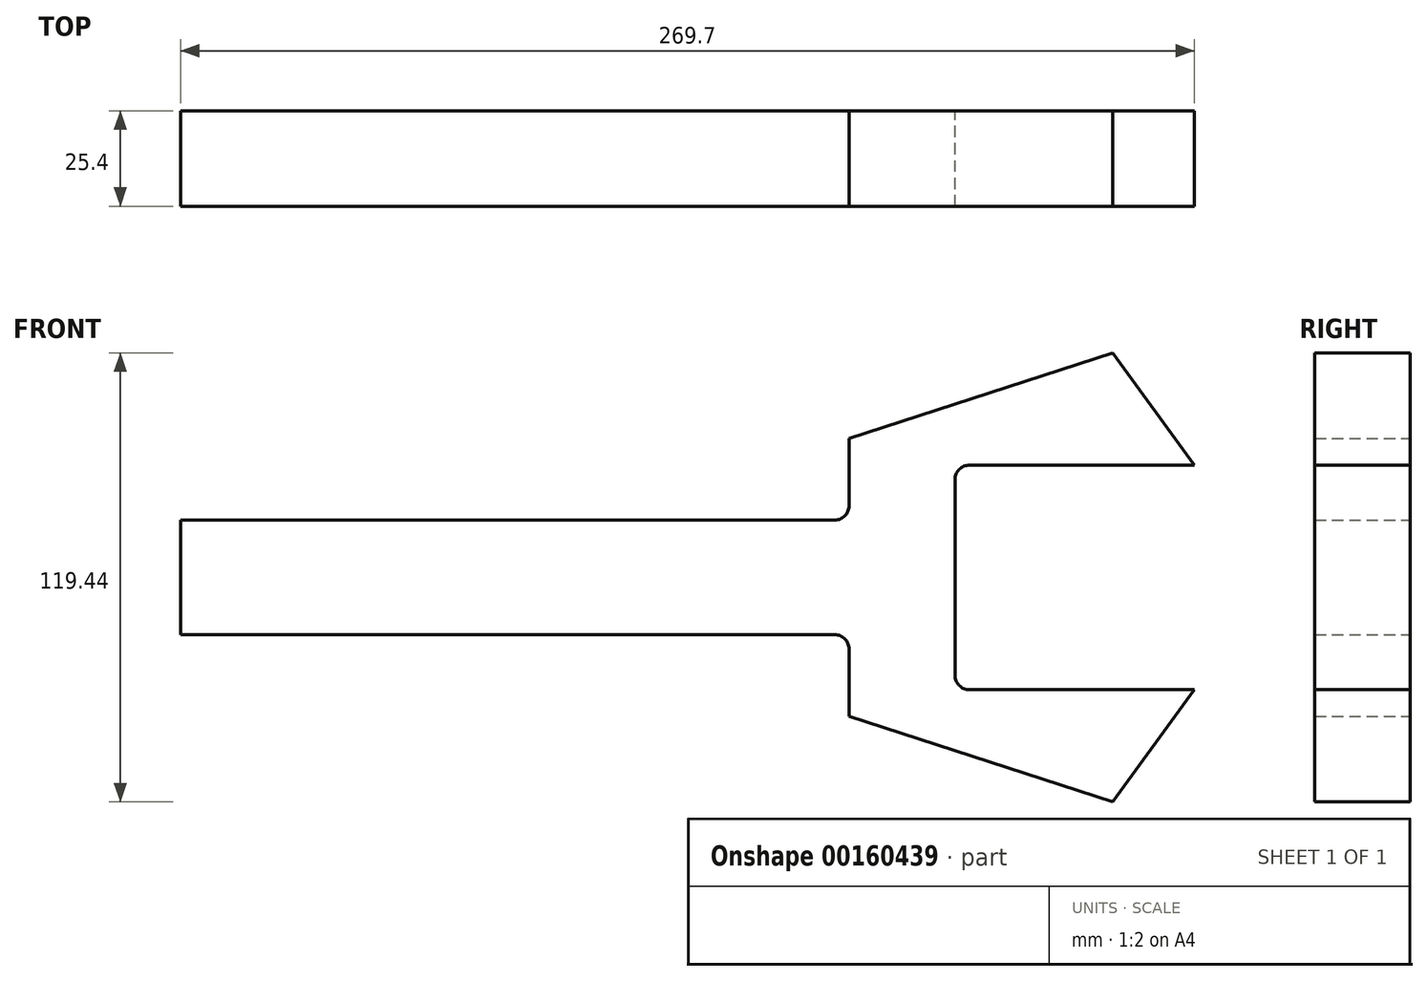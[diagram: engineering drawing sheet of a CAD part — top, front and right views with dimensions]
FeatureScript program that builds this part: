
annotation { "Feature Type Name" : "Feature", "Feature Type Description" : "" }
export const myFeature = defineFeature(function(context is Context, id is Id, definition is map)
    precondition{}
    {
        {
            var Q0;
            Q0=qCreatedBy(makeId("Front.planeOp"),FACE);
            var sketch = newSketch(context, id + "F0", { "sketchPlane" : qUnion([Q0])});
            skArc(sketch, "E0.cCircle", {"start": v(41.1, 29.86) * mm, "mid": v(-50.8, 0) * mm, "end": v(41.1, -29.86) * mm, "construction": true});
            skLineSegment(sketch, "E0.0", {"start": v(-50.8, 19.05) * mm, "end": v(-50.8, 36.9) * mm});
            skLineSegment(sketch, "E0.1", {"start": v(-50.8, 36.9) * mm, "end": v(19.4, 59.72) * mm});
            skLineSegment(sketch, "E0.2", {"start": v(19.4, 59.72) * mm, "end": v(41.1, 29.86) * mm});
            skLineSegment(sketch, "E0.3", {"start": v(41.1, -29.86) * mm, "end": v(19.4, -59.72) * mm});
            skLineSegment(sketch, "E0.4", {"start": v(19.4, -59.72) * mm, "end": v(-50.8, -36.9) * mm});
            skPoint(sketch, "E0.0.midPoint", {"position": v(-50.8, 0) * mm});
            skLineSegment(sketch, "E1.bottom", {"start": v(-54.61, 15.24) * mm, "end": v(-228.6, 15.24) * mm});
            skLineSegment(sketch, "E1.top", {"start": v(-54.61, -15.24) * mm, "end": v(-228.6, -15.24) * mm});
            skLineSegment(sketch, "E1.left", {"start": v(-50.8, 15.24) * mm, "end": v(-50.8, -15.24) * mm});
            skLineSegment(sketch, "E1.right", {"start": v(-228.6, 15.24) * mm, "end": v(-228.6, -15.24) * mm});
            skLineSegment(sketch, "E2", {"start": v(-228.6, 0) * mm, "end": v(-50.8, 0) * mm, "construction": true});
            skPoint(sketch, "E3.newPointA", {"position": v(-50.8, 15.24) * mm});
            skPoint(sketch, "E3.newPointB", {"position": v(-50.8, -36.9) * mm});
            skArc(sketch, "E3.filletArc", {"start": v(-54.61, 15.24) * mm, "mid": v(-51.92, 16.36) * mm, "end": v(-50.8, 19.05) * mm});
            skLineSegment(sketch, "E4", {"start": v(-50.8, -19.05) * mm, "end": v(-50.8, -36.9) * mm});
            skArc(sketch, "E5.filletArc", {"start": v(-50.8, -19.05) * mm, "mid": v(-51.92, -16.36) * mm, "end": v(-54.61, -15.24) * mm});
            skPoint(sketch, "E6.oppositeSnap0", {"position": v(41.1, -29.86) * mm});
            skLineSegment(sketch, "E6.bottom", {"start": v(41.1, 29.86) * mm, "end": v(-18.8, 29.86) * mm});
            skLineSegment(sketch, "E6.top", {"start": v(41.1, -29.86) * mm, "end": v(-18.8, -29.86) * mm});
            skLineSegment(sketch, "E6.right", {"start": v(-22.6, 26.05) * mm, "end": v(-22.6, -26.05) * mm});
            skPoint(sketch, "E7.orphan", {"position": v(62.8, 0) * mm});
            skPoint(sketch, "E8.visualSharp", {"position": v(-22.6, 29.86) * mm});
            skArc(sketch, "E8.filletArc", {"start": v(-18.8, 29.86) * mm, "mid": v(-21.49, 28.74) * mm, "end": v(-22.6, 26.05) * mm});
            skPoint(sketch, "E9.visualSharp", {"position": v(-22.6, -29.86) * mm});
            skArc(sketch, "E9.filletArc", {"start": v(-22.6, -26.05) * mm, "mid": v(-21.49, -28.74) * mm, "end": v(-18.8, -29.86) * mm});
            skSolve(sketch);
        }
        {
            var Q0;
            Q0=makeQuery(id+"F0.imprint","IMPRINT",FACE,{"disambiguationData":[TD([[makeQuery(id+"F0.imprint","IMPRINT",EDGE,{"derivedFrom":sQuery(id+"F0.wireOp",EDGE,"E0.0")}),-1.0]])]});
            extrude(context, id + "F1", {"entities" : qUnion([Q0]), "depth" : 25.4 * mm});
        }
    });
